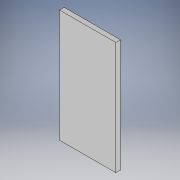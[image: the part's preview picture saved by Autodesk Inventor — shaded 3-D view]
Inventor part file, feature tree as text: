
AUTODESK INVENTOR PART (.ipt)
format: ipt  version: 2018 (Build 220112000, 112)  size: 89,600 bytes
history: native  units: in
note: dims shown in document units (in); Inventor stores cm internally (conversion verified against a paired STEP export)
features: extrude x1, sketch x1
ambient origin geometry x8: Origin, YZ Plane, XZ Plane, XY Plane, X Axis, Y Axis, Z Axis, Center Point
bodies: Solid1 (feature_tree)
feature tree (2):
  extrude  "Extrusion1"  Depth=30.0in
  sketch  "Sketch1"  dims[d0=12.0in d1=30.0in d2=1.0in d3=0.0in]
